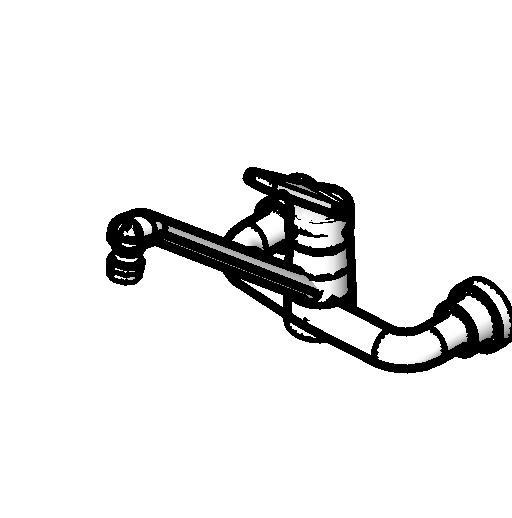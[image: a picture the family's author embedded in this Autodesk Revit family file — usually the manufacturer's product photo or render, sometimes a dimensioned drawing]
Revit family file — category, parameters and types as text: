
# Revit family: Deca_Misturador Cozinha Aspen_1256.C35_Bica Móvel-Mesa
name_source: partatom
category: Plumbing Fixtures
revit_build: Autodesk Revit Architecture 2012 (Build: 20110916_2132(x64)
units: mm (PartAtom-declared; Revit-internal decimal feet)

## types (1)
- 1256.C.35_Cromado CR10
    Aprovado por = Contino/quattroD
    Assembly Code = D2020
    Atendimento ao Cliente = 0800-0117073
    CWFU = 0
    Consumo = Varia com a pressão
    Criado por = Contino/quattroD
    Código = 1256.C.35
    Default Elevation = 0 mm  [stored 0 ft]
    Description = Misturador cozinha mesa
    Diâmetro Água Fria = 15 mm  [stored 0.0492126 ft]
    Diâmetro Água Quente = 15 mm  [stored 0.0492126 ft]
    Flow Pressure = 0.00 psi
    HWFU = 0
    Informações Complementares = Mecanismo: 3 1/2 voltas
    Linha = Aspen
    Louça/Metais = Metal
    Manufacturer = Deca
    Material = Deca_Latão Cromado e Plástico de Engenharia
    Misturador = Deca CR10 Cromado Metal
    Model = 1256.C.35
    Norma = ABNT NBR 11535: 1991
    Peso Liquido (Kg) = 1.5
    Pressão = 2 A 40 mca
    Produto = Misturador Cozinha bica móvel - Mesa
    Raio Água Fria = 8 mm  [stored 0.0262467 ft]
    Raio Água Quente = 8 mm  [stored 0.0262467 ft]
    Segmento = Competitivo
    URL = www.deca.com.br/produtos
    Variações de COR = Cromado (1256.C.35).
    Vendido Separadamente = Ligação Flexível: 30 cm (4607.C.030), 40 cm (4607.C.040), 50 cm (4607.C.050).
    WFU = 0

note: [stored X ft] marks values corroborated as IEEE doubles in the binary element streams (Revit-internal decimal feet)

## geometry (parser evidence)
native form markers: Blend x4, Sweep x1
no freeform markers — native parametric forms only
